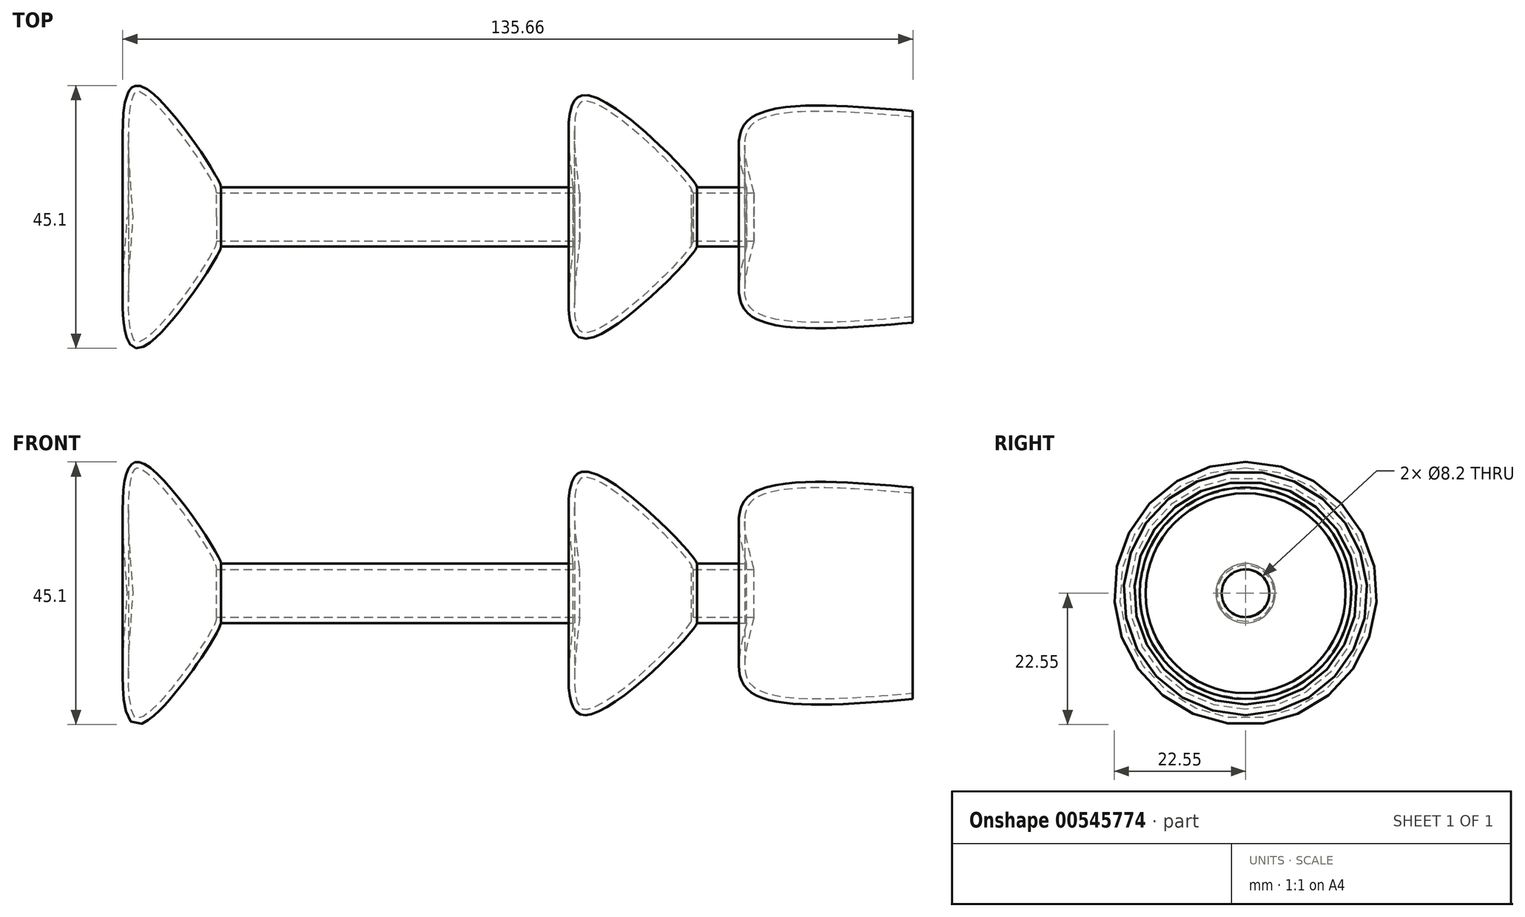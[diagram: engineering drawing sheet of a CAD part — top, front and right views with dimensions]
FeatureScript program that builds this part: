
annotation { "Feature Type Name" : "Feature", "Feature Type Description" : "" }
export const myFeature = defineFeature(function(context is Context, id is Id, definition is map)
    precondition{}
    {
        {
            var Q0;
            Q0=qCreatedBy(makeId("Front.planeOp"),FACE);
            var sketch = newSketch(context, id + "F0", { "sketchPlane" : qUnion([Q0])});
            skFitSpline(sketch, "E0", {"points": [v(-70.35, 0) * mm, v(-67.92, 22.41) * mm, v(-54.26, 5.1) * mm, v(-54.56, 5.1) * mm], "startDerivative": vector(-6.04, 75.61) * mm, "endDerivative": vector(-7.9, 3.41) * mm});
            skLineSegment(sketch, "E1", {"start": v(-54.26, 5.1) * mm, "end": v(6.18, 5.1) * mm});
            skFitSpline(sketch, "E2", {"points": [v(6.18, 5.1) * mm, v(8.6, 20.9) * mm, v(27.44, 5.1) * mm, v(26.83, 5.1) * mm], "startDerivative": vector(-6.84, 59.46) * mm, "endDerivative": vector(-11.69, 3.88) * mm});
            skLineSegment(sketch, "E3", {"start": v(27.44, 5.1) * mm, "end": v(35.94, 5.1) * mm});
            skFitSpline(sketch, "E4", {"points": [v(35.94, 5.1) * mm, v(35.94, 16.34) * mm, v(64.49, 18.16) * mm], "startDerivative": vector(-8.95, 34.21) * mm, "endDerivative": vector(60.71, -5.09) * mm});
            skLineSegment(sketch, "E5", {"start": v(64.49, 18.16) * mm, "end": v(64.49, 0) * mm});
            skLineSegment(sketch, "E6", {"start": v(64.49, 0) * mm, "end": v(0, 0) * mm});
            skLineSegment(sketch, "E7", {"start": v(0, 0) * mm, "end": v(-70.35, 0) * mm});
            skSolve(sketch);
        }
        {
            var Q0;
            {var subQ2=sQuery(id+"F0.wireOp",EDGE,"E1");Q0=makeQuery(id+"F0.imprint","IMPRINT",FACE,{"disambiguationData":[TD([[makeQuery(id+"F0.imprint","IMPRINT",EDGE,{"derivedFrom":subQ2}),-1.0]])]});}
            var Q1;
            Q1=sQuery(id+"F0.wireOp",EDGE,"E7");
            revolve(context, id + "F1", {"entities" : qUnion([Q0]), "axis" : qUnion([Q1]), "revolveType" : RevolveType.FULL});
        }
        {
            var Q0;
            Q0=makeQuery(id+"F1.opRevolve","SWEPT_FACE",FACE,{"disambiguationData":[OSD([sQuery(id+"F0.wireOp",EDGE,"E5")])]});
            shell(context, id + "F2", {"entities" : qUnion([Q0]), "thickness" : 1 * mm});
        }
    });
